# Revit family: HVAC_HangingSystems_Walraven_BIS_RapidRail_Fixing_Rail_WM15
name_source: partatom
category: Mechanical Equipment
revit_build: Autodesk Revit MEP 2016 (Build: 20150220_1215(x64)
units: mm (PartAtom-declared; Revit-internal decimal feet)

## family parameters
Cut with Voids When Loaded = No
OmniClass Number = 23.60.30.11.17
OmniClass Title = Pipework/Ductwork Mechanical Fasteners/Supports
Part Type = Normal
Room Calculation Point = No
Round Connector Dimension = Use Diameter
Shared = No
Work Plane-Based = No

## types (1)
- std
    Assembly Code = 50
    BIMobject category = Hanging Systems
    BIMobject category code = hvac-hanging-systems
    BIMobject main category = HVAC
    BIMobject main category code = hvac
    Brand url = https://www.walraven.com
    Date of publishing = 7/20/2018
    Description = fixing rail
    Design country = Netherlands
    Edition number = 0
    IFC Classification = Mechanical Fastener
    IfcDescription = fixing rail
    IfcExportAs = IfcMechanicalFastenerType
    IfcExportType = USERDEFINED
    Manufacturer = Walraven
    Manufacturer country = Netherlands
    Manufacturer name = Walraven
    Material main = Steel
    Model = BIS RapidRail Fixing Rail WM15
    NLRS_C_code_SfB_tabel1 = 50
    Nominal height = 0 mm  [stored 0 ft]
    Nominal width = 0 mm  [stored 0 ft]
    OmniClass Code = 23-27 43 13
    OmniClass Description = Mechanical Pipe Supports
    Product Guid = a78c6f59-2421-483d-a623-713bce42838b
    Product SKU = bis-rapidrail-fixing-rail-wm15
    Product certification = https://library.walraven.com
    Product data url = https://bimobject.com
    Product family = Rail Systems
    Product group = Fixing Rail
    Product url = https://www.walraven.com
    QR code = http://bimobject.com
    RSen_C_certificates = RAL-GZ 655 approval
    RSen_C_code_ETIM = EC000386
    RSen_C_code_ETIM_url = https://prod.etim-international.com
    RSen_C_content_modification_date = 04-06-2018
    RSen_C_content_releasedate = 22-02-2018
    RSen_C_intended_use = hanging systems
    RSen_C_level_of_development = LOD400
    RSen_C_material = steel
    RSen_C_material_colour = grey
    RSen_C_material_finish = pre-galvanized
    Technical description = https://library.walraven.com
    URL = https://www.walraven.com
    Weight Net (Kg) = 0
    region_index = 1
    type_index = 1

note: [stored X ft] marks values corroborated as IEEE doubles in the binary element streams (Revit-internal decimal feet)

## geometry (parser evidence)
native form markers: Blend x2, Sweep x4
no freeform markers — native parametric forms only
